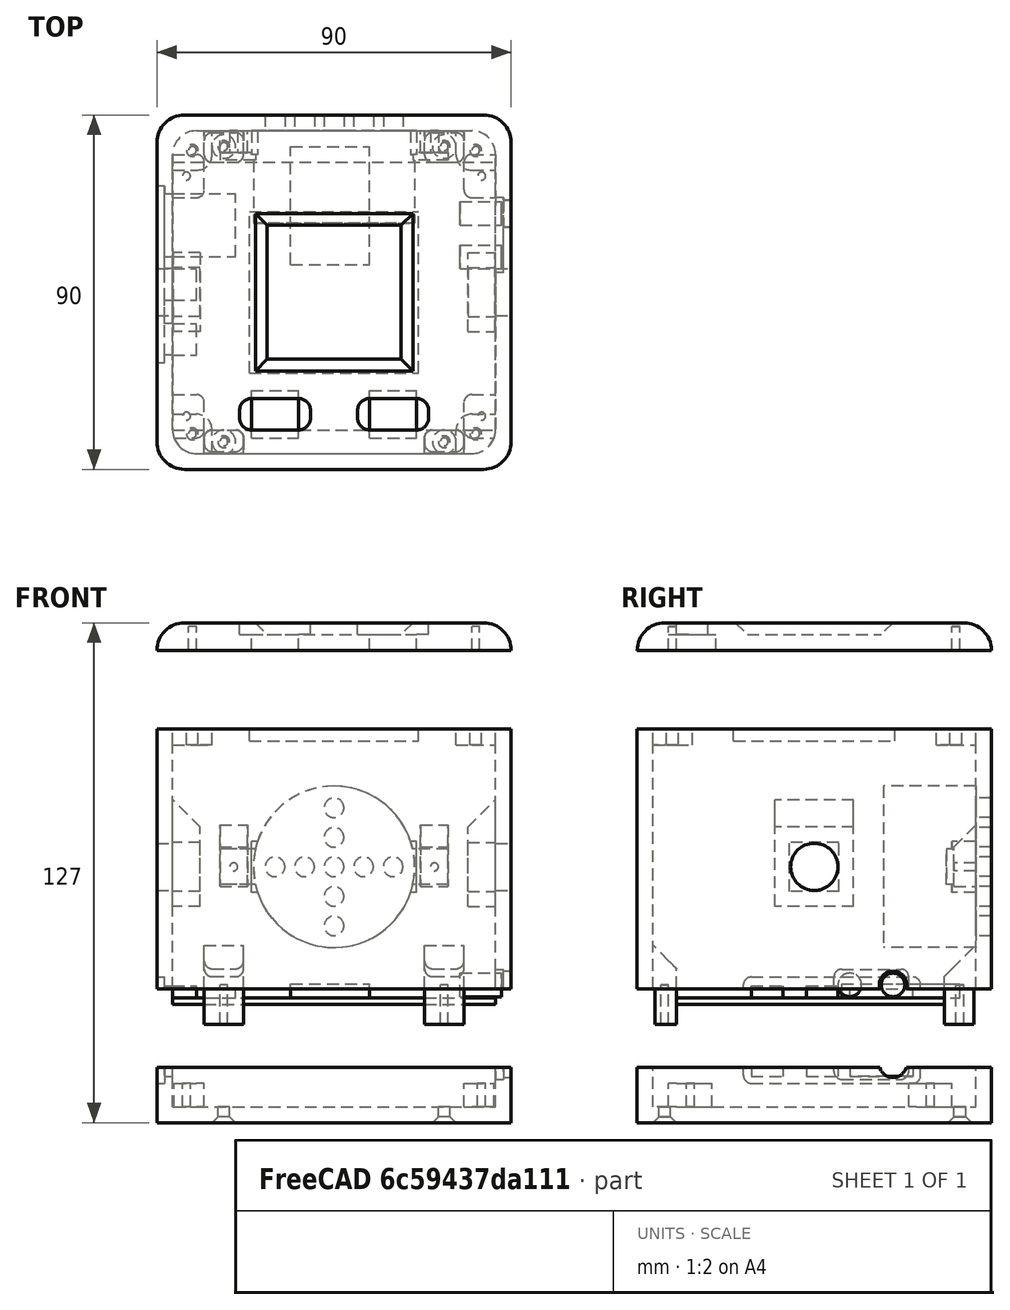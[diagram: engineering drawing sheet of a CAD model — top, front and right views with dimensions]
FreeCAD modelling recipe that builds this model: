
FCSTD DOCUMENT  (FreeCAD 0.18.4R)
Label: tonie-clone
License: All rights reserved
LicenseURL: http://en.wikipedia.org/wiki/All_rights_reserved
objects: Part::Box×54, Part::Cut×48, Part::Cylinder×42, Part::Fillet×24, Part::Chamfer×10, Part::MultiFuse×7, App::DocumentObjectGroup×4, Part::MultiCommon×3, Part::Compound×1
note: 189 computed .brp shape members not serialized (recipe doc carries the construction recipe); baked Part::Feature solids carry a one-line shape summary decoded from their .brp

FEATURE [Part::Box] Box  label="board"
  AttacherType = Attacher::AttachEngine3D
  Height = 1.75
  Length = 82
  Width = 68
FEATURE [Part::Box] Box001  label="esp"
  AttacherType = Attacher::AttachEngine3D
  Height = 3.5
  Length = 20
  Placement = pos=(30,42,1.75) rot=(0,0,1;0rad)
  Width = 30
FEATURE [Part::Box] Box002  label="sd"
  AttacherType = Attacher::AttachEngine3D
  Height = 2.25
  Length = 16
  Placement = pos=(0,44,1.75) rot=(0,0,1;0rad)
  Width = 16
FEATURE [Part::Box] Box003  label="power"
  AttacherType = Attacher::AttachEngine3D
  Height = 3
  Length = 6
  Placement = pos=(0,19,1.75) rot=(0,0,1;0rad)
  Width = 8
FEATURE [Part::Box] Box004  label="rfid-sensor"
  AttacherType = Attacher::AttachEngine3D
  Height = 3
  Length = 43
  Placement = pos=(23.5,24.5,77) rot=(0,0,1;0rad)
  Width = 41
FEATURE [Part::Box] Box005  label="Cube"
  AttacherType = Attacher::AttachEngine3D
  Height = 90
  Length = 90
  Width = 90
FEATURE [Part::Fillet] Fillet
  Base = -> Box005
  Edges = 8 edges r=7: [Edge1,Edge2,Edge3,Edge5,Edge6,Edge7,Edge10,Edge12]
FEATURE [Part::Box] Box006  label="Cube001"
  AttacherType = Attacher::AttachEngine3D
  Height = 82
  Length = 82
  Width = 82
FEATURE [Part::Fillet] Fillet001
  Base = -> Box006
  Edges = 8 edges r=6: [Edge1,Edge2,Edge3,Edge5,Edge6,Edge7,Edge10,Edge12]
  Placement = pos=(4,4,4) rot=(0,0,1;0rad)
FEATURE [Part::Cut] Cut
  Base = -> Fillet
  Tool = -> Fillet001
FEATURE [Part::Cylinder] Cylinder  label="Headphone"
  Angle = 360
  AttacherType = Attacher::AttachEngine3D
  Height = 10.5
  Placement = pos=(73,55,5) rot=(0,1,0;1.5708rad)
  Radius = 3
FEATURE [Part::Cylinder] Cylinder001  label="Microphone"
  Angle = 360
  AttacherType = Attacher::AttachEngine3D
  Height = 10.5
  Placement = pos=(73,44,5) rot=(0,1,0;1.5708rad)
  Radius = 3
FEATURE [Part::Box] Box007  label="Cube002"
  AttacherType = Attacher::AttachEngine3D
  Height = 3
  Length = 40
  Placement = pos=(25,25,84) rot=(0,0,1;0rad)
  Width = 40
FEATURE [Part::Box] Box008  label="Cube003"
  AttacherType = Attacher::AttachEngine3D
  Height = 14
  Length = 90
  Width = 90
FEATURE [Part::MultiCommon] Common
  Shapes = -> [Cut,Box008]
FEATURE [Part::Box] Box009  label="Cube004"
  AttacherType = Attacher::AttachEngine3D
  Height = 6
  Length = 8
  Placement = pos=(4,8,3) rot=(0,0,1;0rad)
  Width = 11
FEATURE [Part::Box] Box010  label="Headphone Cut"
  AttacherType = Attacher::AttachEngine3D
  Height = 8
  Length = 2
  Placement = pos=(86,50,11) rot=(0,0,1;0rad)
  Width = 19
FEATURE [Part::Fillet] Fillet002
  Base = -> Box010
  Edges = 4 edges r=2: [Edge9,Edge10,Edge11,Edge12]
FEATURE [Part::Cut] Cut001
  Base = -> Common
  Tool = -> Fillet002
FEATURE [Part::Cylinder] Cylinder002  label="Headphone001"
  Angle = 360
  AttacherType = Attacher::AttachEngine3D
  Height = 10.5
  Placement = pos=(80,65,15) rot=(0,1,0;1.5708rad)
  Radius = 3.5
FEATURE [Part::Cut] Cut002
  Base = -> Cut001
  Tool = -> Cylinder002
FEATURE [Part::Fillet] Fillet003
  Base = -> Box009
  Edges = 2 edges r=2: [Edge5,Edge7]
  Placement = pos=(0,0,1) rot=(0,0,1;0rad)
FEATURE [Part::Box] Box011  label="Cube005"
  AttacherType = Attacher::AttachEngine3D
  Height = 6
  Length = 8
  Placement = pos=(4,8,3) rot=(0,0,1;0rad)
  Width = 11
FEATURE [Part::Fillet] Fillet004
  Base = -> Box011
  Edges = 2 edges r=2: [Edge5,Edge7]
  Placement = pos=(0,61,1) rot=(0,0,1;0rad)
FEATURE [Part::Box] Box013  label="Cube007"
  AttacherType = Attacher::AttachEngine3D
  Height = 6
  Length = 8
  Placement = pos=(78,8,4) rot=(0,0,1;0rad)
  Width = 11
FEATURE [Part::Fillet] Fillet005
  Base = -> Box013
  Edges = 2 edges r=2: [Edge1,Edge3]
FEATURE [Part::Box] Box014  label="Cube008"
  AttacherType = Attacher::AttachEngine3D
  Height = 6
  Length = 8
  Placement = pos=(78,8,4) rot=(0,0,1;0rad)
  Width = 11
FEATURE [Part::Fillet] Fillet006
  Base = -> Box014
  Edges = 2 edges r=2: [Edge1,Edge3]
  Placement = pos=(0,61,0) rot=(0,0,1;0rad)
FEATURE [Part::Cylinder] Cylinder003  label="Cylinder"
  Angle = 360
  AttacherType = Attacher::AttachEngine3D
  Height = 8
  Placement = pos=(7.5,13.5,4) rot=(0,0,1;0rad)
  Radius = 1
FEATURE [Part::Cylinder] Cylinder004  label="Cylinder001"
  Angle = 360
  AttacherType = Attacher::AttachEngine3D
  Height = 8
  Placement = pos=(7.5,74.5,4) rot=(0,0,1;0rad)
  Radius = 1
FEATURE [Part::Cylinder] Cylinder005  label="Cylinder002"
  Angle = 360
  AttacherType = Attacher::AttachEngine3D
  Height = 8
  Placement = pos=(82.5,74.5,4) rot=(0,0,1;0rad)
  Radius = 1
FEATURE [Part::Cylinder] Cylinder006  label="Cylinder003"
  Angle = 360
  AttacherType = Attacher::AttachEngine3D
  Height = 9
  Placement = pos=(82.5,13.5,4) rot=(0,0,1;0rad)
  Radius = 1
FEATURE [Part::Cut] Cut003
  Base = -> Fillet006
  Tool = -> Cylinder005
FEATURE [Part::Cut] Cut004
  Base = -> Fillet005
  Tool = -> Cylinder006
FEATURE [Part::Cut] Cut005
  Base = -> Fillet004
  Tool = -> Cylinder004
FEATURE [Part::Cut] Cut006
  Base = -> Fillet003
  Tool = -> Cylinder003
FEATURE [Part::Box] Box015  label="sd001"
  AttacherType = Attacher::AttachEngine3D
  Height = 2.25
  Length = 16
  Placement = pos=(0,54,11.75) rot=(0,0,1;0rad)
  Width = 16
FEATURE [Part::Box] Box016  label="uart"
  AttacherType = Attacher::AttachEngine3D
  Height = 3
  Length = 6
  Placement = pos=(0,33,1.75) rot=(0,0,1;0rad)
  Width = 8
FEATURE [Part::Compound] Compound
  Links = -> [Box,Box001,Box002,Box003,Cylinder,Cylinder001,Box016]
  Placement = pos=(4,10,10) rot=(0,0,1;0rad)
FEATURE [Part::Box] Box018  label="power001"
  AttacherType = Attacher::AttachEngine3D
  Height = 3
  Length = 6
  Placement = pos=(0,29,11.75) rot=(0,0,1;0rad)
  Width = 8
FEATURE [Part::Cut] Cut007
  Base = -> Cut002
  Tool = -> Box015
FEATURE [Part::Cut] Cut008
  Base = -> Cut007
  Tool = -> Box018
FEATURE [Part::Box] Box019  label="Cube009"
  AttacherType = Attacher::AttachEngine3D
  Height = 20
  Length = 10
  Placement = pos=(12,4,5) rot=(0,0,1;0rad)
  Width = 6
FEATURE [Part::Box] Box020  label="Cube010"
  AttacherType = Attacher::AttachEngine3D
  Height = 20
  Length = 10
  Placement = pos=(68,4,5) rot=(0,0,1;0rad)
  Width = 6
FEATURE [Part::Box] Box021  label="Cube011"
  AttacherType = Attacher::AttachEngine3D
  Height = 20
  Length = 10
  Placement = pos=(12,78,5) rot=(0,0,1;0rad)
  Width = 8
FEATURE [Part::Box] Box022  label="Cube012"
  AttacherType = Attacher::AttachEngine3D
  Height = 20
  Length = 10
  Placement = pos=(68,78,5) rot=(0,0,1;0rad)
  Width = 8
FEATURE [Part::Cylinder] Cylinder007  label="Cylinder004"
  Angle = 360
  AttacherType = Attacher::AttachEngine3D
  Height = 10
  Placement = pos=(73,7,0) rot=(0,0,1;0rad)
  Radius = 1.5
FEATURE [Part::Cylinder] Cylinder008  label="Cylinder005"
  Angle = 360
  AttacherType = Attacher::AttachEngine3D
  Height = 10
  Placement = pos=(17,7,0) rot=(0,0,1;0rad)
  Radius = 1.5
FEATURE [Part::Cylinder] Cylinder009  label="Cylinder006"
  Angle = 360
  AttacherType = Attacher::AttachEngine3D
  Height = 10
  Placement = pos=(17,82,0) rot=(0,0,1;0rad)
  Radius = 1.5
FEATURE [Part::Cylinder] Cylinder010  label="Cylinder007"
  Angle = 360
  AttacherType = Attacher::AttachEngine3D
  Height = 10
  Placement = pos=(73,82,0) rot=(0,0,1;0rad)
  Radius = 1.5
FEATURE [Part::Cut] Cut009
  Base = -> Cut008
  Tool = -> Cylinder007
FEATURE [Part::Cut] Cut010
  Base = -> Cut009
  Tool = -> Cylinder010
FEATURE [Part::Cut] Cut011
  Base = -> Cut010
  Tool = -> Cylinder009
FEATURE [Part::Cut] Cut012
  Base = -> Cut011
  Tool = -> Cylinder008
FEATURE [Part::Cylinder] Cylinder011  label="Cylinder008"
  Angle = 360
  AttacherType = Attacher::AttachEngine3D
  Height = 10
  Placement = pos=(73,7,5) rot=(0,0,1;0rad)
  Radius = 1
FEATURE [Part::Cylinder] Cylinder012  label="Cylinder011"
  Angle = 360
  AttacherType = Attacher::AttachEngine3D
  Height = 10
  Placement = pos=(73,82,5) rot=(0,0,1;0rad)
  Radius = 1
FEATURE [Part::Cylinder] Cylinder013  label="Cylinder012"
  Angle = 360
  AttacherType = Attacher::AttachEngine3D
  Height = 10
  Placement = pos=(17,82,5) rot=(0,0,1;0rad)
  Radius = 1
FEATURE [Part::Cylinder] Cylinder014  label="Cylinder013"
  Angle = 360
  AttacherType = Attacher::AttachEngine3D
  Height = 10
  Placement = pos=(17,7,5) rot=(0,0,1;0rad)
  Radius = 1
FEATURE [Part::Box] Box023  label="uart001"
  AttacherType = Attacher::AttachEngine3D
  Height = 3
  Length = 6
  Placement = pos=(0,43,11.75) rot=(0,0,1;0rad)
  Width = 8
FEATURE [Part::Cut] Cut013
  Base = -> Cut012
  Tool = -> Box023
FEATURE [Part::Box] Box024  label="Headphone Cut001"
  AttacherType = Attacher::AttachEngine3D
  Height = 8
  Length = 2
  Placement = pos=(0,27,10) rot=(0,0,1;0rad)
  Width = 45
FEATURE [Part::Fillet] Fillet007
  Base = -> Box024
  Edges = 4 edges r=2: [Edge9,Edge10,Edge11,Edge12]
FEATURE [Part::Cut] Cut014
  Base = -> Cut013
  Tool = -> Fillet007
FEATURE [Part::Chamfer] Chamfer
  Base = -> Cut014
  Edges = 4 edges r=1.5: [Edge59,Edge60,Edge61,Edge62]
FEATURE [Part::MultiFuse] Fusion  label="bottom001"
  Placement = pos=(0,0,-20) rot=(0,0,1;0rad)
  Shapes = -> [Chamfer,Cut003,Cut004,Cut005,Cut006]
FEATURE [App::DocumentObjectGroup] Group002  label="bottom"
  Group = -> [Fusion]
FEATURE [Part::Box] Box026  label="Cube014"
  AttacherType = Attacher::AttachEngine3D
  Height = 66
  Length = 90
  Placement = pos=(0,0,14) rot=(0,0,1;0rad)
  Width = 90
FEATURE [Part::Box] Box027  label="Cube015"
  AttacherType = Attacher::AttachEngine3D
  Height = 90
  Length = 90
  Width = 90
FEATURE [Part::Fillet] Fillet010
  Base = -> Box027
  Edges = 8 edges r=7: [Edge1,Edge2,Edge3,Edge5,Edge6,Edge7,Edge10,Edge12]
FEATURE [Part::Box] Box028  label="sd002"
  AttacherType = Attacher::AttachEngine3D
  Height = 2.25
  Length = 16
  Placement = pos=(0,54,11.75) rot=(0,0,1;0rad)
  Width = 16
FEATURE [Part::Box] Box029  label="Cube016"
  AttacherType = Attacher::AttachEngine3D
  Height = 82
  Length = 82
  Width = 82
FEATURE [Part::Fillet] Fillet011
  Base = -> Box029
  Edges = 8 edges r=6: [Edge1,Edge2,Edge3,Edge5,Edge6,Edge7,Edge10,Edge12]
  Placement = pos=(4,4,4) rot=(0,0,1;0rad)
FEATURE [Part::Cut] Cut016
  Base = -> Fillet010
  Tool = -> Fillet011
FEATURE [Part::MultiCommon] Common001
  Shapes = -> [Cut016,Box026]
FEATURE [Part::Box] Box030  label="Headphone Cut002"
  AttacherType = Attacher::AttachEngine3D
  Height = 8
  Length = 2
  Placement = pos=(86,50,11) rot=(0,0,1;0rad)
  Width = 19
FEATURE [Part::Fillet] Fillet008
  Base = -> Box030
  Edges = 4 edges r=2: [Edge9,Edge10,Edge11,Edge12]
FEATURE [Part::Cylinder] Cylinder015  label="Headphone002"
  Angle = 360
  AttacherType = Attacher::AttachEngine3D
  Height = 10.5
  Placement = pos=(80,65,15) rot=(0,1,0;1.5708rad)
  Radius = 3.5
FEATURE [Part::Cut] Cut019
  Base = -> Common001
  Tool = -> Fillet008
FEATURE [Part::Cut] Cut018
  Base = -> Cut019
  Tool = -> Cylinder015
FEATURE [Part::Box] Box033  label="Headphone Cut003"
  AttacherType = Attacher::AttachEngine3D
  Height = 7
  Length = 2
  Placement = pos=(0,27,10) rot=(0,0,1;0rad)
  Width = 45
FEATURE [Part::Box] Box035  label="power002"
  AttacherType = Attacher::AttachEngine3D
  Height = 3
  Length = 6
  Placement = pos=(0,29,11.75) rot=(0,0,1;0rad)
  Width = 8
FEATURE [Part::Cut] Cut024
  Base = -> Cut018
  Tool = -> Box028
FEATURE [Part::Cut] Cut025
  Base = -> Cut024
  Tool = -> Box035
FEATURE [Part::Cylinder] Cylinder020  label="Cylinder018"
  Angle = 360
  AttacherType = Attacher::AttachEngine3D
  Height = 10
  Placement = pos=(73,7,0) rot=(0,0,1;0rad)
  Radius = 1.5
FEATURE [Part::Cylinder] Cylinder021  label="Cylinder019"
  Angle = 360
  AttacherType = Attacher::AttachEngine3D
  Height = 10
  Placement = pos=(17,82,0) rot=(0,0,1;0rad)
  Radius = 1.5
FEATURE [Part::Cylinder] Cylinder022  label="Cylinder020"
  Angle = 360
  AttacherType = Attacher::AttachEngine3D
  Height = 10
  Placement = pos=(73,82,0) rot=(0,0,1;0rad)
  Radius = 1.5
FEATURE [Part::Cylinder] Cylinder023  label="Cylinder021"
  Angle = 360
  AttacherType = Attacher::AttachEngine3D
  Height = 10
  Placement = pos=(17,7,0) rot=(0,0,1;0rad)
  Radius = 1.5
FEATURE [Part::Cut] Cut029
  Base = -> Cut025
  Tool = -> Cylinder020
FEATURE [Part::Cut] Cut028
  Base = -> Cut029
  Tool = -> Cylinder022
FEATURE [Part::Cut] Cut027
  Base = -> Cut028
  Tool = -> Cylinder021
FEATURE [Part::Cut] Cut026
  Base = -> Cut027
  Tool = -> Cylinder023
FEATURE [Part::Fillet] Fillet015
  Base = -> Box033
  Edges = 4 edges r=2: [Edge9,Edge10,Edge11,Edge12]
FEATURE [Part::Box] Box036  label="uart002"
  AttacherType = Attacher::AttachEngine3D
  Height = 3
  Length = 6
  Placement = pos=(0,43,11.75) rot=(0,0,1;0rad)
  Width = 8
FEATURE [Part::Cut] Cut023
  Base = -> Cut026
  Tool = -> Box036
FEATURE [Part::Cut] Cut020
  Base = -> Cut023
  Tool = -> Fillet015
FEATURE [Part::Box] Box037  label="Cube017"
  AttacherType = Attacher::AttachEngine3D
  Height = 10
  Length = 10
  Placement = pos=(12,85.5,4) rot=(0,0,1;0rad)
  Width = 0.5
FEATURE [Part::Box] Box038  label="Cube018"
  AttacherType = Attacher::AttachEngine3D
  Height = 10
  Length = 10
  Placement = pos=(68,85.5,4) rot=(0,0,1;0rad)
  Width = 0.5
FEATURE [Part::Box] Box039  label="Cube019"
  AttacherType = Attacher::AttachEngine3D
  Height = 10
  Length = 10
  Placement = pos=(12,4,4) rot=(0,0,1;0rad)
  Width = 0.5
FEATURE [Part::Box] Box040  label="Cube020"
  AttacherType = Attacher::AttachEngine3D
  Height = 10
  Length = 10
  Placement = pos=(68,4,4) rot=(0,0,1;0rad)
  Width = 0.5
FEATURE [Part::Chamfer] Chamfer001
  Base = -> Box020
  Edges = 1 edges r=5.9: [Edge12]
FEATURE [Part::Chamfer] Chamfer002
  Base = -> Box019
  Edges = 1 edges r=5.9: [Edge12]
FEATURE [Part::Chamfer] Chamfer003
  Base = -> Box021
  Edges = 1 edges r=7.9: [Edge10]
FEATURE [Part::Chamfer] Chamfer004
  Base = -> Box022
  Edges = 1 edges r=7.9: [Edge10]
FEATURE [Part::Cut] Cut030
  Base = -> Chamfer001
  Tool = -> Cylinder011
FEATURE [Part::Cut] Cut031
  Base = -> Chamfer002
  Tool = -> Cylinder014
FEATURE [Part::Cut] Cut032
  Base = -> Chamfer003
  Tool = -> Cylinder013
FEATURE [Part::Cut] Cut033
  Base = -> Chamfer004
  Tool = -> Cylinder012
FEATURE [Part::Cut] Cut034
  Base = -> Cut030
  Tool = -> Box040
FEATURE [Part::Cut] Cut035
  Base = -> Cut033
  Tool = -> Box038
FEATURE [Part::Cut] Cut036
  Base = -> Cut032
  Tool = -> Box037
FEATURE [Part::Cut] Cut037  label="Cut072"
  Base = -> Cut031
  Tool = -> Box039
FEATURE [Part::Fillet] Fillet016
  Base = -> Cut036
  Edges = 4 edges r=2: [Edge5,Edge7,Edge17,Edge22]
FEATURE [Part::Fillet] Fillet017
  Base = -> Cut035
  Edges = 4 edges r=2: [Edge5,Edge7,Edge17,Edge22]
FEATURE [Part::Fillet] Fillet018
  Base = -> Cut037
  Edges = 4 edges r=2: [Edge2,Edge4,Edge11,Edge16]
FEATURE [Part::Fillet] Fillet019
  Base = -> Cut034
  Edges = 4 edges r=2: [Edge2,Edge4,Edge11,Edge16]
FEATURE [Part::Cylinder] Cylinder024  label="Cylinder022"
  Angle = 360
  AttacherType = Attacher::AttachEngine3D
  Height = 23.5
  Radius = 20.5
FEATURE [Part::Box] Box042  label="Cube022"
  AttacherType = Attacher::AttachEngine3D
  Height = 6
  Length = 13
  Placement = pos=(-6.5,-21,0) rot=(0,0,1;0rad)
  Width = 42
FEATURE [Part::Box] Box043  label="Cube023"
  AttacherType = Attacher::AttachEngine3D
  Height = 2
  Length = 9
  Placement = pos=(-4.5,-29,5.5) rot=(0,0,1;0rad)
  Width = 58
FEATURE [Part::MultiFuse] Fusion001  label="Speaker"
  Placement = pos=(45,86,45) rot=(0.57735,-0.57735,0.57735;2.0944rad)
  Shapes = -> [Cylinder024,Box042,Box043]
FEATURE [App::DocumentObjectGroup] Group  label="Parts"
  Group = -> [Box,Box001,Box002,Box003,Cylinder,Cylinder001,Compound,Box016,Box004,Fusion001]
FEATURE [Part::Cylinder] Cylinder025  label="Cylinder023"
  Angle = 360
  AttacherType = Attacher::AttachEngine3D
  Height = 4
  Placement = pos=(45,90,45) rot=(1,0,0;1.5708rad)
  Radius = 2.5
FEATURE [Part::Cylinder] Cylinder026  label="Cylinder024"
  Angle = 360
  AttacherType = Attacher::AttachEngine3D
  Height = 4
  Placement = pos=(60,90,45) rot=(1,0,0;1.5708rad)
  Radius = 2.5
FEATURE [Part::Cylinder] Cylinder027  label="Cylinder025"
  Angle = 360
  AttacherType = Attacher::AttachEngine3D
  Height = 4
  Placement = pos=(30,90,45) rot=(1,0,0;1.5708rad)
  Radius = 2.5
FEATURE [Part::Cylinder] Cylinder028  label="Cylinder026"
  Angle = 360
  AttacherType = Attacher::AttachEngine3D
  Height = 4
  Placement = pos=(45,90,60) rot=(1,0,0;1.5708rad)
  Radius = 2.5
FEATURE [Part::Cylinder] Cylinder029  label="Cylinder027"
  Angle = 360
  AttacherType = Attacher::AttachEngine3D
  Height = 4
  Placement = pos=(45,90,30) rot=(1,0,0;1.5708rad)
  Radius = 2.5
FEATURE [Part::Cylinder] Cylinder030  label="Cylinder028"
  Angle = 360
  AttacherType = Attacher::AttachEngine3D
  Height = 4
  Placement = pos=(45,90,52.5) rot=(1,0,0;1.5708rad)
  Radius = 2.5
FEATURE [Part::Cylinder] Cylinder031  label="Cylinder029"
  Angle = 360
  AttacherType = Attacher::AttachEngine3D
  Height = 4
  Placement = pos=(45,90,37.5) rot=(1,0,0;1.5708rad)
  Radius = 2.5
FEATURE [Part::Cylinder] Cylinder032  label="Cylinder030"
  Angle = 360
  AttacherType = Attacher::AttachEngine3D
  Height = 4
  Placement = pos=(37.5,90,45) rot=(1,0,0;1.5708rad)
  Radius = 2.5
FEATURE [Part::Cylinder] Cylinder033  label="Cylinder031"
  Angle = 360
  AttacherType = Attacher::AttachEngine3D
  Height = 4
  Placement = pos=(52.5,90,45) rot=(1,0,0;1.5708rad)
  Radius = 2.5
FEATURE [Part::MultiFuse] Fusion002
  Shapes = -> [Cylinder025,Cylinder032,Cylinder026,Cylinder029,Cylinder031,Cylinder027,Cylinder028,Cylinder033,Cylinder030]
FEATURE [Part::Cut] Cut038
  Base = -> Cut020
  Tool = -> Fusion002
FEATURE [Part::Box] Box044  label="Cube024"
  AttacherType = Attacher::AttachEngine3D
  Height = 16
  Length = 7
  Placement = pos=(16,80.5,40) rot=(0,0,1;0rad)
  Width = 6
FEATURE [Part::Chamfer] Chamfer005
  Base = -> Box044
  Edges = 1 edges r=5.9: [Edge10]
FEATURE [Part::Box] Box045  label="Cube025"
  AttacherType = Attacher::AttachEngine3D
  Height = 16
  Length = 7
  Placement = pos=(67,80.5,40) rot=(0,0,1;0rad)
  Width = 6
FEATURE [Part::Chamfer] Chamfer006
  Base = -> Box045
  Edges = 1 edges r=5.9: [Edge10]
FEATURE [Part::Cylinder] Cylinder034  label="Cylinder032"
  Angle = 360
  AttacherType = Attacher::AttachEngine3D
  Height = 4
  Placement = pos=(0,45,45) rot=(0,1,0;1.5708rad)
  Radius = 6
FEATURE [Part::Cylinder] Cylinder035  label="Cylinder033"
  Angle = 360
  AttacherType = Attacher::AttachEngine3D
  Height = 4
  Placement = pos=(86,45,45) rot=(0,1,0;1.5708rad)
  Radius = 6
FEATURE [Part::MultiFuse] Fusion003
  Shapes = -> [Cylinder035,Cylinder034]
FEATURE [Part::Cut] Cut039
  Base = -> Cut038
  Tool = -> Fusion003
FEATURE [Part::Box] Box046  label="Cube026"
  AttacherType = Attacher::AttachEngine3D
  Height = 27
  Length = 7
  Placement = pos=(79,35,35) rot=(0,0,1;0rad)
  Width = 20
FEATURE [Part::Box] Box047  label="Cube027"
  AttacherType = Attacher::AttachEngine3D
  Height = 12.5
  Length = 8
  Placement = pos=(78,38.75,38.75) rot=(0,0,1;0rad)
  Width = 12.5
FEATURE [Part::Cut] Cut040
  Base = -> Box046
  Tool = -> Box047
FEATURE [Part::Chamfer] Chamfer007
  Base = -> Cut040
  Edges = 1 edges r=6.9: [Edge2]
FEATURE [Part::Box] Box048  label="Cube028"
  AttacherType = Attacher::AttachEngine3D
  Height = 27
  Length = 7
  Placement = pos=(79,35,35) rot=(0,0,1;0rad)
  Width = 20
FEATURE [Part::Box] Box049  label="Cube029"
  AttacherType = Attacher::AttachEngine3D
  Height = 12.5
  Length = 8
  Placement = pos=(78,38.75,38.75) rot=(0,0,1;0rad)
  Width = 12.5
FEATURE [Part::Cut] Cut041
  Base = -> Box048
  Tool = -> Box049
FEATURE [Part::Chamfer] Chamfer008
  Base = -> Cut041
  Edges = 1 edges r=6.9: [Edge2]
  Placement = pos=(90,90,0) rot=(0,0,1;3.14159rad)
FEATURE [Part::Cylinder] Cylinder036  label="Cylinder034"
  Angle = 360
  AttacherType = Attacher::AttachEngine3D
  Height = 10
  Placement = pos=(70.5,89,45) rot=(1,0,0;1.5708rad)
  Radius = 1
FEATURE [Part::Cylinder] Cylinder037  label="Cylinder035"
  Angle = 360
  AttacherType = Attacher::AttachEngine3D
  Height = 10
  Placement = pos=(19.5,89,45) rot=(1,0,0;1.5708rad)
  Radius = 1
FEATURE [Part::Cut] Cut042
  Base = -> Chamfer005
  Tool = -> Cylinder037
FEATURE [Part::Cut] Cut043
  Base = -> Chamfer006
  Tool = -> Cylinder036
FEATURE [Part::Box] Box050  label="Cube030"
  AttacherType = Attacher::AttachEngine3D
  Height = 4
  Length = 10
  Placement = pos=(4,4,76) rot=(0,0,1;0rad)
  Width = 10
FEATURE [Part::Fillet] Fillet020
  Base = -> Box050
  Edges = 1 edges r=4: [Edge7]
FEATURE [Part::Box] Box051  label="Cube031"
  AttacherType = Attacher::AttachEngine3D
  Height = 4
  Length = 10
  Placement = pos=(76,4,76) rot=(0,0,1;0rad)
  Width = 10
FEATURE [Part::Fillet] Fillet021
  Base = -> Box051
  Edges = 1 edges r=4: [Edge3]
FEATURE [Part::Box] Box052  label="Cube032"
  AttacherType = Attacher::AttachEngine3D
  Height = 4
  Length = 10
  Placement = pos=(4,76,76) rot=(0,0,1;0rad)
  Width = 10
FEATURE [Part::Fillet] Fillet022
  Base = -> Box052
  Edges = 1 edges r=4: [Edge5]
FEATURE [Part::Box] Box053  label="Cube033"
  AttacherType = Attacher::AttachEngine3D
  Height = 4
  Length = 10
  Placement = pos=(76,76,76) rot=(0,0,1;0rad)
  Width = 10
FEATURE [Part::Fillet] Fillet023
  Base = -> Box053
  Edges = 1 edges r=4: [Edge1]
FEATURE [Part::Cylinder] Cylinder038  label="Cylinder036"
  Angle = 360
  AttacherType = Attacher::AttachEngine3D
  Height = 8
  Placement = pos=(9,9,72) rot=(0,0,1;0rad)
  Radius = 1.5
FEATURE [Part::Cylinder] Cylinder039  label="Cylinder037"
  Angle = 360
  AttacherType = Attacher::AttachEngine3D
  Height = 8
  Placement = pos=(81,9,72) rot=(0,0,1;0rad)
  Radius = 1.5
FEATURE [Part::Cylinder] Cylinder040  label="Cylinder038"
  Angle = 360
  AttacherType = Attacher::AttachEngine3D
  Height = 8
  Placement = pos=(9,81,72) rot=(0,0,1;0rad)
  Radius = 1.5
FEATURE [Part::Cylinder] Cylinder041  label="Cylinder039"
  Angle = 360
  AttacherType = Attacher::AttachEngine3D
  Height = 8
  Placement = pos=(81,81,72) rot=(0,0,1;0rad)
  Radius = 1.5
FEATURE [Part::Cut] Cut044
  Base = -> Fillet023
  Tool = -> Cylinder041
FEATURE [Part::Cut] Cut045
  Base = -> Fillet022
  Tool = -> Cylinder040
FEATURE [Part::Cut] Cut046
  Base = -> Fillet021
  Tool = -> Cylinder039
FEATURE [Part::Cut] Cut047
  Base = -> Fillet020
  Tool = -> Cylinder038
FEATURE [Part::MultiFuse] Fusion004  label="middle001"
  Shapes = -> [Fillet016,Chamfer007,Cut039,Cut045,Chamfer008,Fillet017,Cut042,Fillet019,Cut047,Cut043,Cut044,Cut046,Fillet018]
FEATURE [App::DocumentObjectGroup] Group001  label="middle"
  Group = -> [Box020,Box019,Box022,Box021,Cut034,Cut035,Cut036,Cut037,Fusion004]
FEATURE [Part::Cylinder] Cylinder050  label="Cylinder053"
  Angle = 360
  AttacherType = Attacher::AttachEngine3D
  Height = 8
  Placement = pos=(9,81,78) rot=(0,0,1;0rad)
  Radius = 1
FEATURE [Part::Cylinder] Cylinder053  label="Cylinder058"
  Angle = 360
  AttacherType = Attacher::AttachEngine3D
  Height = 8
  Placement = pos=(9,9,78) rot=(0,0,1;0rad)
  Radius = 1
FEATURE [Part::Box] Box063  label="Cube040"
  AttacherType = Attacher::AttachEngine3D
  Height = 75
  Length = 82
  Width = 82
FEATURE [Part::Fillet] Fillet030
  Base = -> Box063
  Edges = 8 edges r=6: [Edge1,Edge2,Edge3,Edge5,Edge6,Edge7,Edge10,Edge12]
  Placement = pos=(4,4,4) rot=(0,0,1;0rad)
FEATURE [Part::Box] Box064  label="Cube041"
  AttacherType = Attacher::AttachEngine3D
  Height = 87
  Length = 90
  Width = 90
FEATURE [Part::Fillet] Fillet028
  Base = -> Box064
  Edges = 8 edges r=7: [Edge1,Edge2,Edge3,Edge5,Edge6,Edge7,Edge10,Edge12]
FEATURE [Part::Cut] Cut069
  Base = -> Fillet028
  Tool = -> Fillet030
FEATURE [Part::Box] Box065  label="Cube042"
  AttacherType = Attacher::AttachEngine3D
  Height = 66
  Length = 90
  Placement = pos=(0,0,80) rot=(0,0,1;0rad)
  Width = 90
FEATURE [Part::MultiCommon] Common002
  Shapes = -> [Cut069,Box065]
FEATURE [Part::Cylinder] Cylinder060  label="Cylinder064"
  Angle = 360
  AttacherType = Attacher::AttachEngine3D
  Height = 8
  Placement = pos=(81,9,78) rot=(0,0,1;0rad)
  Radius = 1
FEATURE [Part::Cylinder] Cylinder063  label="Cylinder060"
  Angle = 360
  AttacherType = Attacher::AttachEngine3D
  Height = 8
  Placement = pos=(81,81,78) rot=(0,0,1;0rad)
  Radius = 1
FEATURE [Part::Chamfer] Chamfer009
  Base = -> Box007
  Edges = 4 edges r=2.99: [Edge4,Edge8,Edge9,Edge11]
FEATURE [Part::Cut] Cut070
  Base = -> Common002
  Tool = -> Chamfer009
FEATURE [Part::MultiFuse] Fusion005
  Shapes = -> [Cylinder050,Cylinder053,Cylinder063,Cylinder060]
FEATURE [Part::Cut] Cut071
  Base = -> Cut070
  Tool = -> Fusion005
FEATURE [Part::Box] Box066  label="Cube043"
  AttacherType = Attacher::AttachEngine3D
  Height = 4
  Length = 12
  Placement = pos=(24,8,80) rot=(0,0,1;0rad)
  Width = 12
FEATURE [Part::Box] Box067  label="Cube044"
  AttacherType = Attacher::AttachEngine3D
  Height = 4
  Length = 12
  Placement = pos=(54,8,80) rot=(0,0,1;0rad)
  Width = 12
FEATURE [Part::Box] Box068  label="Cube045"
  AttacherType = Attacher::AttachEngine3D
  Height = 3
  Length = 18
  Placement = pos=(51,10,84) rot=(0,0,1;0rad)
  Width = 8
FEATURE [Part::Box] Box069  label="Cube046"
  AttacherType = Attacher::AttachEngine3D
  Height = 3
  Length = 18
  Placement = pos=(21,10,84) rot=(0,0,1;0rad)
  Width = 8
FEATURE [Part::Fillet] Fillet031
  Base = -> Box069
  Edges = 4 edges r=3: [Edge1,Edge3,Edge5,Edge7]
FEATURE [Part::Fillet] Fillet032
  Base = -> Box068
  Edges = 4 edges r=3: [Edge1,Edge3,Edge5,Edge7]
FEATURE [Part::MultiFuse] Fusion006
  Shapes = -> [Box066,Box067,Fillet031,Fillet032]
FEATURE [Part::Cut] Cut072  label="top001"
  Base = -> Cut071
  Placement = pos=(0,0,20) rot=(0,0,1;0rad)
  Tool = -> Fusion006
FEATURE [App::DocumentObjectGroup] Group003  label="top"
  Group = -> [Cut072]
